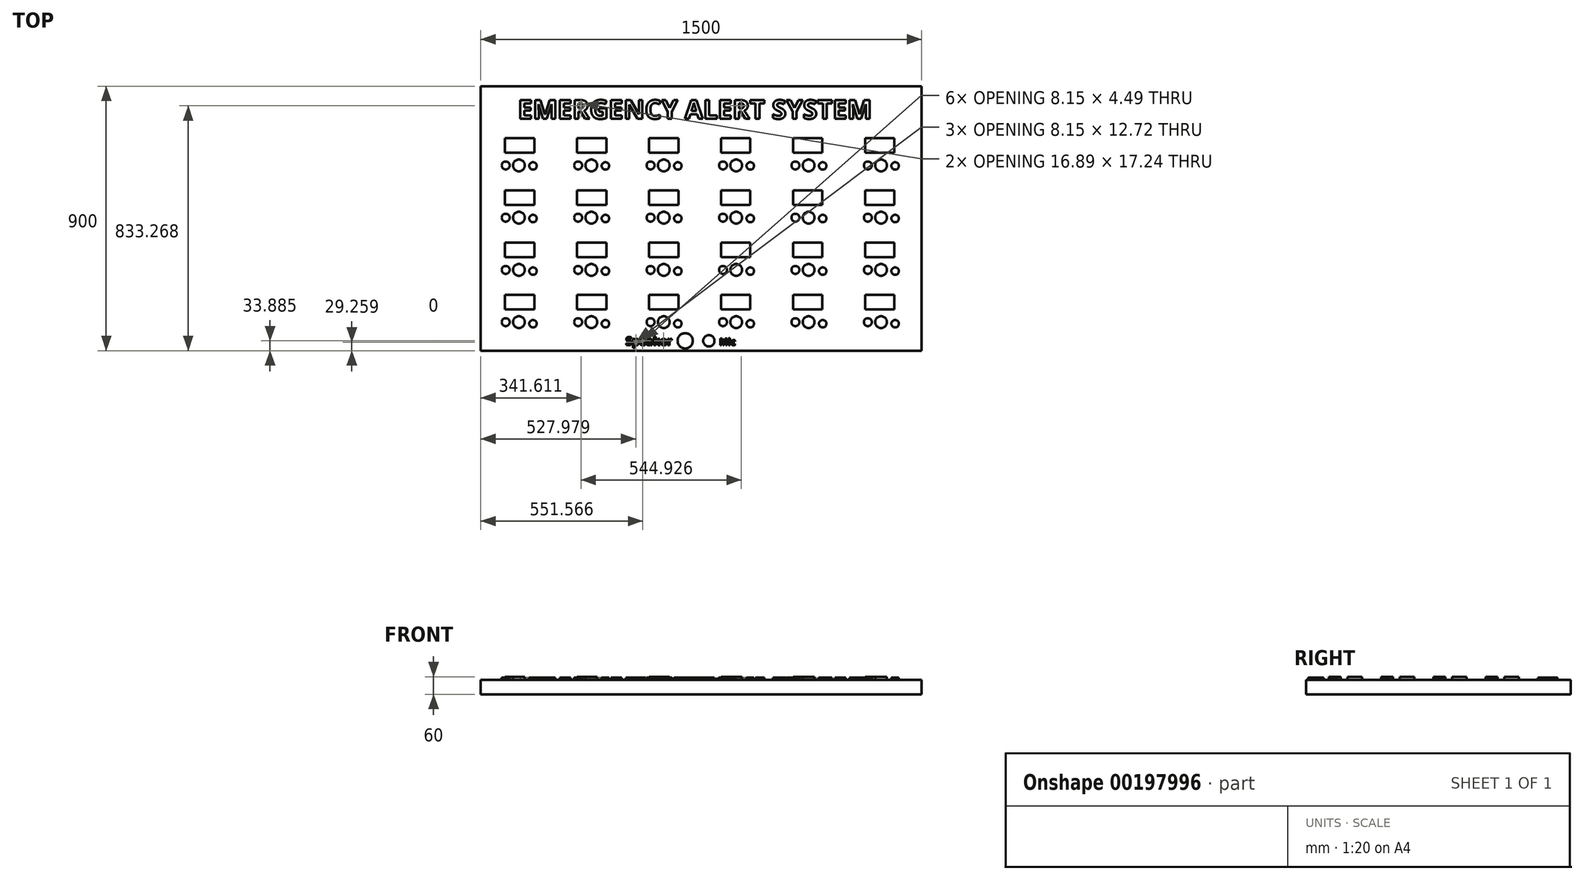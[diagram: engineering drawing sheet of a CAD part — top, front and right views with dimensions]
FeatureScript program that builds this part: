
annotation { "Feature Type Name" : "Feature", "Feature Type Description" : "" }
export const myFeature = defineFeature(function(context is Context, id is Id, definition is map)
    precondition{}
    {
        {
            var Q0;
            Q0=qCreatedBy(makeId("Top.planeOp"),FACE);
            var sketch = newSketch(context, id + "F0", { "sketchPlane" : qUnion([Q0])});
            skLineSegment(sketch, "E0.bottom", {"start": v(-750, 450) * mm, "end": v(750, 450) * mm});
            skLineSegment(sketch, "E0.top", {"start": v(-750, -450) * mm, "end": v(750, -450) * mm});
            skLineSegment(sketch, "E0.left", {"start": v(-750, 450) * mm, "end": v(-750, -450) * mm});
            skLineSegment(sketch, "E0.right", {"start": v(750, 450) * mm, "end": v(750, -450) * mm});
            skPoint(sketch, "E0.middle", {"position": v(0, 0) * mm});
            skSolve(sketch);
        }
        {
            var Q0;
            Q0=makeQuery(id+"F0.imprint","IMPRINT",FACE,{"disambiguationData":[TD([[makeQuery(id+"F0.imprint","IMPRINT",EDGE,{"derivedFrom":sQuery(id+"F0.wireOp",EDGE,"E0.bottom")}),-1.0]])]});
            extrude(context, id + "F1", {"entities" : qUnion([Q0]), "depth" : 50 * mm});
        }
        {
            var Q0;
            Q0=makeQuery(id+"F1.opExtrude","CAP_FACE",FACE,{"disambiguationData":[OSD([sQuery(id+"F0.wireOp",EDGE,"E0.bottom"),sQuery(id+"F0.wireOp",EDGE,"E0.top"),sQuery(id+"F0.wireOp",EDGE,"E0.left"),sQuery(id+"F0.wireOp",EDGE,"E0.right")])],"isStart":false});
            var sketch = newSketch(context, id + "F2", { "sketchPlane" : qUnion([Q0])});
            skLineSegment(sketch, "E1.bottom", {"start": v(-667.65, 273.63) * mm, "end": v(-567.65, 273.63) * mm});
            skLineSegment(sketch, "E1.top", {"start": v(-667.65, 223.63) * mm, "end": v(-567.65, 223.63) * mm});
            skLineSegment(sketch, "E1.left", {"start": v(-667.65, 273.63) * mm, "end": v(-667.65, 223.63) * mm});
            skLineSegment(sketch, "E1.right", {"start": v(-567.65, 273.63) * mm, "end": v(-567.65, 223.63) * mm});
            skLineSegment(sketch, "E2.0.1.0", {"start": v(-667.65, 95.83) * mm, "end": v(-567.65, 95.83) * mm});
            skLineSegment(sketch, "E2.0.1.1", {"start": v(-567.65, 95.83) * mm, "end": v(-567.65, 45.83) * mm});
            skLineSegment(sketch, "E2.0.1.2", {"start": v(-667.65, 45.83) * mm, "end": v(-567.65, 45.83) * mm});
            skLineSegment(sketch, "E2.0.1.3", {"start": v(-667.65, 95.83) * mm, "end": v(-667.65, 45.83) * mm});
            skLineSegment(sketch, "E2.0.2.0", {"start": v(-667.65, -81.97) * mm, "end": v(-567.65, -81.97) * mm});
            skLineSegment(sketch, "E2.0.2.1", {"start": v(-567.65, -81.97) * mm, "end": v(-567.65, -131.97) * mm});
            skLineSegment(sketch, "E2.0.2.2", {"start": v(-667.65, -131.97) * mm, "end": v(-567.65, -131.97) * mm});
            skLineSegment(sketch, "E2.0.2.3", {"start": v(-667.65, -81.97) * mm, "end": v(-667.65, -131.97) * mm});
            skLineSegment(sketch, "E2.0.3.0", {"start": v(-667.65, -259.77) * mm, "end": v(-567.65, -259.77) * mm});
            skLineSegment(sketch, "E2.0.3.1", {"start": v(-567.65, -259.77) * mm, "end": v(-567.65, -309.77) * mm});
            skLineSegment(sketch, "E2.0.3.2", {"start": v(-667.65, -309.77) * mm, "end": v(-567.65, -309.77) * mm});
            skLineSegment(sketch, "E2.0.3.3", {"start": v(-667.65, -259.77) * mm, "end": v(-667.65, -309.77) * mm});
            skLineSegment(sketch, "E2.1.0.0", {"start": v(-422.65, 273.63) * mm, "end": v(-322.65, 273.63) * mm});
            skLineSegment(sketch, "E2.1.0.1", {"start": v(-322.65, 273.63) * mm, "end": v(-322.65, 223.63) * mm});
            skLineSegment(sketch, "E2.1.0.2", {"start": v(-422.65, 223.63) * mm, "end": v(-322.65, 223.63) * mm});
            skLineSegment(sketch, "E2.1.0.3", {"start": v(-422.65, 273.63) * mm, "end": v(-422.65, 223.63) * mm});
            skLineSegment(sketch, "E2.1.1.0", {"start": v(-422.65, 95.83) * mm, "end": v(-322.65, 95.83) * mm});
            skLineSegment(sketch, "E2.1.1.1", {"start": v(-322.65, 95.83) * mm, "end": v(-322.65, 45.83) * mm});
            skLineSegment(sketch, "E2.1.1.2", {"start": v(-422.65, 45.83) * mm, "end": v(-322.65, 45.83) * mm});
            skLineSegment(sketch, "E2.1.1.3", {"start": v(-422.65, 95.83) * mm, "end": v(-422.65, 45.83) * mm});
            skLineSegment(sketch, "E2.1.2.0", {"start": v(-422.65, -81.97) * mm, "end": v(-322.65, -81.97) * mm});
            skLineSegment(sketch, "E2.1.2.1", {"start": v(-322.65, -81.97) * mm, "end": v(-322.65, -131.97) * mm});
            skLineSegment(sketch, "E2.1.2.2", {"start": v(-422.65, -131.97) * mm, "end": v(-322.65, -131.97) * mm});
            skLineSegment(sketch, "E2.1.2.3", {"start": v(-422.65, -81.97) * mm, "end": v(-422.65, -131.97) * mm});
            skLineSegment(sketch, "E2.1.3.0", {"start": v(-422.65, -259.77) * mm, "end": v(-322.65, -259.77) * mm});
            skLineSegment(sketch, "E2.1.3.1", {"start": v(-322.65, -259.77) * mm, "end": v(-322.65, -309.77) * mm});
            skLineSegment(sketch, "E2.1.3.2", {"start": v(-422.65, -309.77) * mm, "end": v(-322.65, -309.77) * mm});
            skLineSegment(sketch, "E2.1.3.3", {"start": v(-422.65, -259.77) * mm, "end": v(-422.65, -309.77) * mm});
            skLineSegment(sketch, "E2.2.0.0", {"start": v(-177.65, 273.63) * mm, "end": v(-77.65, 273.63) * mm});
            skLineSegment(sketch, "E2.2.0.1", {"start": v(-77.65, 273.63) * mm, "end": v(-77.65, 223.63) * mm});
            skLineSegment(sketch, "E2.2.0.2", {"start": v(-177.65, 223.63) * mm, "end": v(-77.65, 223.63) * mm});
            skLineSegment(sketch, "E2.2.0.3", {"start": v(-177.65, 273.63) * mm, "end": v(-177.65, 223.63) * mm});
            skLineSegment(sketch, "E2.2.1.0", {"start": v(-177.65, 95.83) * mm, "end": v(-77.65, 95.83) * mm});
            skLineSegment(sketch, "E2.2.1.1", {"start": v(-77.65, 95.83) * mm, "end": v(-77.65, 45.83) * mm});
            skLineSegment(sketch, "E2.2.1.2", {"start": v(-177.65, 45.83) * mm, "end": v(-77.65, 45.83) * mm});
            skLineSegment(sketch, "E2.2.1.3", {"start": v(-177.65, 95.83) * mm, "end": v(-177.65, 45.83) * mm});
            skLineSegment(sketch, "E2.2.2.0", {"start": v(-177.65, -81.97) * mm, "end": v(-77.65, -81.97) * mm});
            skLineSegment(sketch, "E2.2.2.1", {"start": v(-77.65, -81.97) * mm, "end": v(-77.65, -131.97) * mm});
            skLineSegment(sketch, "E2.2.2.2", {"start": v(-177.65, -131.97) * mm, "end": v(-77.65, -131.97) * mm});
            skLineSegment(sketch, "E2.2.2.3", {"start": v(-177.65, -81.97) * mm, "end": v(-177.65, -131.97) * mm});
            skLineSegment(sketch, "E2.2.3.0", {"start": v(-177.65, -259.77) * mm, "end": v(-77.65, -259.77) * mm});
            skLineSegment(sketch, "E2.2.3.1", {"start": v(-77.65, -259.77) * mm, "end": v(-77.65, -309.77) * mm});
            skLineSegment(sketch, "E2.2.3.2", {"start": v(-177.65, -309.77) * mm, "end": v(-77.65, -309.77) * mm});
            skLineSegment(sketch, "E2.2.3.3", {"start": v(-177.65, -259.77) * mm, "end": v(-177.65, -309.77) * mm});
            skLineSegment(sketch, "E2.3.0.0", {"start": v(67.35, 273.63) * mm, "end": v(167.35, 273.63) * mm});
            skLineSegment(sketch, "E2.3.0.1", {"start": v(167.35, 273.63) * mm, "end": v(167.35, 223.63) * mm});
            skLineSegment(sketch, "E2.3.0.2", {"start": v(67.35, 223.63) * mm, "end": v(167.35, 223.63) * mm});
            skLineSegment(sketch, "E2.3.0.3", {"start": v(67.35, 273.63) * mm, "end": v(67.35, 223.63) * mm});
            skLineSegment(sketch, "E2.3.1.0", {"start": v(67.35, 95.83) * mm, "end": v(167.35, 95.83) * mm});
            skLineSegment(sketch, "E2.3.1.1", {"start": v(167.35, 95.83) * mm, "end": v(167.35, 45.83) * mm});
            skLineSegment(sketch, "E2.3.1.2", {"start": v(67.35, 45.83) * mm, "end": v(167.35, 45.83) * mm});
            skLineSegment(sketch, "E2.3.1.3", {"start": v(67.35, 95.83) * mm, "end": v(67.35, 45.83) * mm});
            skLineSegment(sketch, "E2.3.2.0", {"start": v(67.35, -81.97) * mm, "end": v(167.35, -81.97) * mm});
            skLineSegment(sketch, "E2.3.2.1", {"start": v(167.35, -81.97) * mm, "end": v(167.35, -131.97) * mm});
            skLineSegment(sketch, "E2.3.2.2", {"start": v(67.35, -131.97) * mm, "end": v(167.35, -131.97) * mm});
            skLineSegment(sketch, "E2.3.2.3", {"start": v(67.35, -81.97) * mm, "end": v(67.35, -131.97) * mm});
            skLineSegment(sketch, "E2.3.3.0", {"start": v(67.35, -259.77) * mm, "end": v(167.35, -259.77) * mm});
            skLineSegment(sketch, "E2.3.3.1", {"start": v(167.35, -259.77) * mm, "end": v(167.35, -309.77) * mm});
            skLineSegment(sketch, "E2.3.3.2", {"start": v(67.35, -309.77) * mm, "end": v(167.35, -309.77) * mm});
            skLineSegment(sketch, "E2.3.3.3", {"start": v(67.35, -259.77) * mm, "end": v(67.35, -309.77) * mm});
            skLineSegment(sketch, "E2.4.0.0", {"start": v(312.35, 273.63) * mm, "end": v(412.35, 273.63) * mm});
            skLineSegment(sketch, "E2.4.0.1", {"start": v(412.35, 273.63) * mm, "end": v(412.35, 223.63) * mm});
            skLineSegment(sketch, "E2.4.0.2", {"start": v(312.35, 223.63) * mm, "end": v(412.35, 223.63) * mm});
            skLineSegment(sketch, "E2.4.0.3", {"start": v(312.35, 273.63) * mm, "end": v(312.35, 223.63) * mm});
            skLineSegment(sketch, "E2.4.1.0", {"start": v(312.35, 95.83) * mm, "end": v(412.35, 95.83) * mm});
            skLineSegment(sketch, "E2.4.1.1", {"start": v(412.35, 95.83) * mm, "end": v(412.35, 45.83) * mm});
            skLineSegment(sketch, "E2.4.1.2", {"start": v(312.35, 45.83) * mm, "end": v(412.35, 45.83) * mm});
            skLineSegment(sketch, "E2.4.1.3", {"start": v(312.35, 95.83) * mm, "end": v(312.35, 45.83) * mm});
            skLineSegment(sketch, "E2.4.2.0", {"start": v(312.35, -81.97) * mm, "end": v(412.35, -81.97) * mm});
            skLineSegment(sketch, "E2.4.2.1", {"start": v(412.35, -81.97) * mm, "end": v(412.35, -131.97) * mm});
            skLineSegment(sketch, "E2.4.2.2", {"start": v(312.35, -131.97) * mm, "end": v(412.35, -131.97) * mm});
            skLineSegment(sketch, "E2.4.2.3", {"start": v(312.35, -81.97) * mm, "end": v(312.35, -131.97) * mm});
            skLineSegment(sketch, "E2.4.3.0", {"start": v(312.35, -259.77) * mm, "end": v(412.35, -259.77) * mm});
            skLineSegment(sketch, "E2.4.3.1", {"start": v(412.35, -259.77) * mm, "end": v(412.35, -309.77) * mm});
            skLineSegment(sketch, "E2.4.3.2", {"start": v(312.35, -309.77) * mm, "end": v(412.35, -309.77) * mm});
            skLineSegment(sketch, "E2.4.3.3", {"start": v(312.35, -259.77) * mm, "end": v(312.35, -309.77) * mm});
            skLineSegment(sketch, "E2.5.0.0", {"start": v(557.35, 273.63) * mm, "end": v(657.35, 273.63) * mm});
            skLineSegment(sketch, "E2.5.0.1", {"start": v(657.35, 273.63) * mm, "end": v(657.35, 223.63) * mm});
            skLineSegment(sketch, "E2.5.0.2", {"start": v(557.35, 223.63) * mm, "end": v(657.35, 223.63) * mm});
            skLineSegment(sketch, "E2.5.0.3", {"start": v(557.35, 273.63) * mm, "end": v(557.35, 223.63) * mm});
            skLineSegment(sketch, "E2.5.1.0", {"start": v(557.35, 95.83) * mm, "end": v(657.35, 95.83) * mm});
            skLineSegment(sketch, "E2.5.1.1", {"start": v(657.35, 95.83) * mm, "end": v(657.35, 45.83) * mm});
            skLineSegment(sketch, "E2.5.1.2", {"start": v(557.35, 45.83) * mm, "end": v(657.35, 45.83) * mm});
            skLineSegment(sketch, "E2.5.1.3", {"start": v(557.35, 95.83) * mm, "end": v(557.35, 45.83) * mm});
            skLineSegment(sketch, "E2.5.2.0", {"start": v(557.35, -81.97) * mm, "end": v(657.35, -81.97) * mm});
            skLineSegment(sketch, "E2.5.2.1", {"start": v(657.35, -81.97) * mm, "end": v(657.35, -131.97) * mm});
            skLineSegment(sketch, "E2.5.2.2", {"start": v(557.35, -131.97) * mm, "end": v(657.35, -131.97) * mm});
            skLineSegment(sketch, "E2.5.2.3", {"start": v(557.35, -81.97) * mm, "end": v(557.35, -131.97) * mm});
            skLineSegment(sketch, "E2.5.3.0", {"start": v(557.35, -259.77) * mm, "end": v(657.35, -259.77) * mm});
            skLineSegment(sketch, "E2.5.3.1", {"start": v(657.35, -259.77) * mm, "end": v(657.35, -309.77) * mm});
            skLineSegment(sketch, "E2.5.3.2", {"start": v(557.35, -309.77) * mm, "end": v(657.35, -309.77) * mm});
            skLineSegment(sketch, "E2.5.3.3", {"start": v(557.35, -259.77) * mm, "end": v(557.35, -309.77) * mm});
            skLineSegment(sketch, "E2.direction1", {"start": v(-667.65, 273.63) * mm, "end": v(-422.65, 273.63) * mm, "construction": true});
            skLineSegment(sketch, "E2.direction2", {"start": v(-667.65, 273.63) * mm, "end": v(-667.65, 95.83) * mm, "construction": true});
            skSolve(sketch);
        }
        {
            var Q0;
            Q0=qSketchRegion(id+"F2",true);
            extrude(context, id + "F3", {"entities" : qUnion([Q0]), "depth" : 10 * mm});
        }
        {
            var Q0;
            Q0=makeQuery(id+"F1.opExtrude","CAP_FACE",FACE,{"disambiguationData":[OSD([sQuery(id+"F0.wireOp",EDGE,"E0.bottom"),sQuery(id+"F0.wireOp",EDGE,"E0.top"),sQuery(id+"F0.wireOp",EDGE,"E0.left"),sQuery(id+"F0.wireOp",EDGE,"E0.right")])],"isStart":false});
            var sketch = newSketch(context, id + "F4", { "sketchPlane" : qUnion([Q0])});
            skCircle(sketch, "E3", {"center": v(-619.9, 180.43) * mm, "radius": 20.14 * mm});
            skCircle(sketch, "E4.0.1.0", {"center": v(-619.9, 2.63) * mm, "radius": 20.14 * mm});
            skCircle(sketch, "E4.0.2.0", {"center": v(-619.9, -175.17) * mm, "radius": 20.14 * mm});
            skCircle(sketch, "E4.0.3.0", {"center": v(-619.9, -352.97) * mm, "radius": 20.14 * mm});
            skCircle(sketch, "E4.1.0.0", {"center": v(-373.51, 180.43) * mm, "radius": 20.14 * mm});
            skCircle(sketch, "E4.1.1.0", {"center": v(-373.51, 2.63) * mm, "radius": 20.14 * mm});
            skCircle(sketch, "E4.1.2.0", {"center": v(-373.51, -175.17) * mm, "radius": 20.14 * mm});
            skCircle(sketch, "E4.1.3.0", {"center": v(-373.51, -352.97) * mm, "radius": 20.14 * mm});
            skCircle(sketch, "E4.2.0.0", {"center": v(-127.13, 180.43) * mm, "radius": 20.14 * mm});
            skCircle(sketch, "E4.2.1.0", {"center": v(-127.13, 2.63) * mm, "radius": 20.14 * mm});
            skCircle(sketch, "E4.2.2.0", {"center": v(-127.13, -175.17) * mm, "radius": 20.14 * mm});
            skCircle(sketch, "E4.2.3.0", {"center": v(-127.13, -352.97) * mm, "radius": 20.14 * mm});
            skCircle(sketch, "E4.3.0.0", {"center": v(119.25, 180.43) * mm, "radius": 20.14 * mm});
            skCircle(sketch, "E4.3.1.0", {"center": v(119.25, 2.63) * mm, "radius": 20.14 * mm});
            skCircle(sketch, "E4.3.2.0", {"center": v(119.25, -175.17) * mm, "radius": 20.14 * mm});
            skCircle(sketch, "E4.3.3.0", {"center": v(119.25, -352.97) * mm, "radius": 20.14 * mm});
            skCircle(sketch, "E4.4.0.0", {"center": v(365.63, 180.43) * mm, "radius": 20.14 * mm});
            skCircle(sketch, "E4.4.1.0", {"center": v(365.63, 2.63) * mm, "radius": 20.14 * mm});
            skCircle(sketch, "E4.4.2.0", {"center": v(365.63, -175.17) * mm, "radius": 20.14 * mm});
            skCircle(sketch, "E4.4.3.0", {"center": v(365.63, -352.97) * mm, "radius": 20.14 * mm});
            skCircle(sketch, "E4.5.0.0", {"center": v(612, 180.43) * mm, "radius": 20.14 * mm});
            skCircle(sketch, "E4.5.1.0", {"center": v(612, 2.63) * mm, "radius": 20.14 * mm});
            skCircle(sketch, "E4.5.2.0", {"center": v(612, -175.17) * mm, "radius": 20.14 * mm});
            skCircle(sketch, "E4.5.3.0", {"center": v(612, -352.97) * mm, "radius": 20.14 * mm});
            skLineSegment(sketch, "E4.direction1", {"start": v(-619.9, 180.43) * mm, "end": v(-373.51, 180.43) * mm, "construction": true});
            skLineSegment(sketch, "E4.direction2", {"start": v(-619.9, 180.43) * mm, "end": v(-619.9, 2.63) * mm, "construction": true});
            skSolve(sketch);
        }
        {
            var Q0;
            Q0=qSketchRegion(id+"F4",true);
            extrude(context, id + "F5", {"entities" : qUnion([Q0]), "depth" : 10 * mm});
        }
        {
            var Q0;
            Q0=makeQuery(id+"F1.opExtrude","CAP_FACE",FACE,{"disambiguationData":[OSD([sQuery(id+"F0.wireOp",EDGE,"E0.bottom"),sQuery(id+"F0.wireOp",EDGE,"E0.top"),sQuery(id+"F0.wireOp",EDGE,"E0.left"),sQuery(id+"F0.wireOp",EDGE,"E0.right")])],"isStart":false});
            var sketch = newSketch(context, id + "F6", { "sketchPlane" : qUnion([Q0])});
            skSolve(sketch);
        }
        {
            var Q0;
            Q0=makeQuery(id+"F6.imprint","IMPRINT",FACE,{"disambiguationData":[TD([[makeQuery(id+"F6.imprint","IMPRINT",EDGE,{"derivedFrom":makeQuery(id+"F1.opExtrude","CAP_EDGE",EDGE,{"disambiguationData":[OSD([sQuery(id+"F0.wireOp",EDGE,"E0.bottom")])],"isStart":false})}),-1.0]])]});
            var sketch = newSketch(context, id + "F7", { "sketchPlane" : qUnion([Q0])});
            skCircle(sketch, "E5", {"center": v(-571.98, 178.93) * mm, "radius": 12.7 * mm});
            skCircle(sketch, "E6.0.1.0", {"center": v(-571.98, -0.14) * mm, "radius": 12.7 * mm});
            skCircle(sketch, "E6.0.2.0", {"center": v(-571.98, -179.2) * mm, "radius": 12.7 * mm});
            skCircle(sketch, "E6.0.3.0", {"center": v(-571.98, -358.28) * mm, "radius": 12.7 * mm});
            skCircle(sketch, "E6.1.0.0", {"center": v(-325.6, 178.93) * mm, "radius": 12.7 * mm});
            skCircle(sketch, "E6.1.1.0", {"center": v(-325.6, -0.14) * mm, "radius": 12.7 * mm});
            skCircle(sketch, "E6.1.2.0", {"center": v(-325.6, -179.2) * mm, "radius": 12.7 * mm});
            skCircle(sketch, "E6.1.3.0", {"center": v(-325.6, -358.28) * mm, "radius": 12.7 * mm});
            skCircle(sketch, "E6.2.0.0", {"center": v(-79.22, 178.93) * mm, "radius": 12.7 * mm});
            skCircle(sketch, "E6.2.1.0", {"center": v(-79.22, -0.14) * mm, "radius": 12.7 * mm});
            skCircle(sketch, "E6.2.2.0", {"center": v(-79.22, -179.2) * mm, "radius": 12.7 * mm});
            skCircle(sketch, "E6.2.3.0", {"center": v(-79.22, -358.28) * mm, "radius": 12.7 * mm});
            skCircle(sketch, "E6.3.0.0", {"center": v(167.16, 178.93) * mm, "radius": 12.7 * mm});
            skCircle(sketch, "E6.3.1.0", {"center": v(167.16, -0.14) * mm, "radius": 12.7 * mm});
            skCircle(sketch, "E6.3.2.0", {"center": v(167.16, -179.2) * mm, "radius": 12.7 * mm});
            skCircle(sketch, "E6.3.3.0", {"center": v(167.16, -358.28) * mm, "radius": 12.7 * mm});
            skCircle(sketch, "E6.4.0.0", {"center": v(413.54, 178.93) * mm, "radius": 12.7 * mm});
            skCircle(sketch, "E6.4.1.0", {"center": v(413.54, -0.14) * mm, "radius": 12.7 * mm});
            skCircle(sketch, "E6.4.2.0", {"center": v(413.54, -179.2) * mm, "radius": 12.7 * mm});
            skCircle(sketch, "E6.4.3.0", {"center": v(413.54, -358.28) * mm, "radius": 12.7 * mm});
            skCircle(sketch, "E6.5.0.0", {"center": v(659.92, 178.93) * mm, "radius": 12.7 * mm});
            skCircle(sketch, "E6.5.1.0", {"center": v(659.92, -0.14) * mm, "radius": 12.7 * mm});
            skCircle(sketch, "E6.5.2.0", {"center": v(659.92, -179.2) * mm, "radius": 12.7 * mm});
            skCircle(sketch, "E6.5.3.0", {"center": v(659.92, -358.28) * mm, "radius": 12.7 * mm});
            skLineSegment(sketch, "E6.direction1", {"start": v(-571.98, 178.93) * mm, "end": v(-325.6, 178.93) * mm, "construction": true});
            skLineSegment(sketch, "E6.direction2", {"start": v(-571.98, 178.93) * mm, "end": v(-571.98, -0.14) * mm, "construction": true});
            skSolve(sketch);
        }
        {
            var Q0;
            Q0=qSketchRegion(id+"F7",true);
            extrude(context, id + "F8", {"entities" : qUnion([Q0]), "depth" : 7 * mm});
        }
        {
            var Q0;
            Q0=makeQuery(id+"F6.imprint","IMPRINT",FACE,{"disambiguationData":[TD([[makeQuery(id+"F6.imprint","IMPRINT",EDGE,{"derivedFrom":makeQuery(id+"F1.opExtrude","CAP_EDGE",EDGE,{"disambiguationData":[OSD([sQuery(id+"F0.wireOp",EDGE,"E0.bottom")])],"isStart":false})}),-1.0]])]});
            var sketch = newSketch(context, id + "F9", { "sketchPlane" : qUnion([Q0])});
            skCircle(sketch, "E7", {"center": v(-664.81, 180.43) * mm, "radius": 13.56 * mm});
            skCircle(sketch, "E8.0.1.0", {"center": v(-664.81, 2.63) * mm, "radius": 13.56 * mm});
            skCircle(sketch, "E8.0.2.0", {"center": v(-664.81, -175.17) * mm, "radius": 13.56 * mm});
            skCircle(sketch, "E8.0.3.0", {"center": v(-664.81, -352.97) * mm, "radius": 13.56 * mm});
            skCircle(sketch, "E8.1.0.0", {"center": v(-418.43, 180.43) * mm, "radius": 13.56 * mm});
            skCircle(sketch, "E8.1.1.0", {"center": v(-418.43, 2.63) * mm, "radius": 13.56 * mm});
            skCircle(sketch, "E8.1.2.0", {"center": v(-418.43, -175.17) * mm, "radius": 13.56 * mm});
            skCircle(sketch, "E8.1.3.0", {"center": v(-418.43, -352.97) * mm, "radius": 13.56 * mm});
            skCircle(sketch, "E8.2.0.0", {"center": v(-172.05, 180.43) * mm, "radius": 13.56 * mm});
            skCircle(sketch, "E8.2.1.0", {"center": v(-172.05, 2.63) * mm, "radius": 13.56 * mm});
            skCircle(sketch, "E8.2.2.0", {"center": v(-172.05, -175.17) * mm, "radius": 13.56 * mm});
            skCircle(sketch, "E8.2.3.0", {"center": v(-172.05, -352.97) * mm, "radius": 13.56 * mm});
            skCircle(sketch, "E8.3.0.0", {"center": v(74.33, 180.43) * mm, "radius": 13.56 * mm});
            skCircle(sketch, "E8.3.1.0", {"center": v(74.33, 2.63) * mm, "radius": 13.56 * mm});
            skCircle(sketch, "E8.3.2.0", {"center": v(74.33, -175.17) * mm, "radius": 13.56 * mm});
            skCircle(sketch, "E8.3.3.0", {"center": v(74.33, -352.97) * mm, "radius": 13.56 * mm});
            skCircle(sketch, "E8.4.0.0", {"center": v(320.7, 180.43) * mm, "radius": 13.56 * mm});
            skCircle(sketch, "E8.4.1.0", {"center": v(320.7, 2.63) * mm, "radius": 13.56 * mm});
            skCircle(sketch, "E8.4.2.0", {"center": v(320.7, -175.17) * mm, "radius": 13.56 * mm});
            skCircle(sketch, "E8.4.3.0", {"center": v(320.7, -352.97) * mm, "radius": 13.56 * mm});
            skCircle(sketch, "E8.5.0.0", {"center": v(567.09, 180.43) * mm, "radius": 13.56 * mm});
            skCircle(sketch, "E8.5.1.0", {"center": v(567.09, 2.63) * mm, "radius": 13.56 * mm});
            skCircle(sketch, "E8.5.2.0", {"center": v(567.09, -175.17) * mm, "radius": 13.56 * mm});
            skCircle(sketch, "E8.5.3.0", {"center": v(567.09, -352.97) * mm, "radius": 13.56 * mm});
            skLineSegment(sketch, "E8.direction1", {"start": v(-664.81, 180.43) * mm, "end": v(-418.43, 180.43) * mm, "construction": true});
            skLineSegment(sketch, "E8.direction2", {"start": v(-664.81, 180.43) * mm, "end": v(-664.81, 2.63) * mm, "construction": true});
            skSolve(sketch);
        }
        {
            var Q0;
            Q0=qSketchRegion(id+"F9",true);
            extrude(context, id + "F10", {"entities" : qUnion([Q0]), "depth" : 7 * mm});
        }
        {
            var Q0;
            Q0=makeQuery(id+"F6.imprint","IMPRINT",FACE,{"disambiguationData":[TD([[makeQuery(id+"F6.imprint","IMPRINT",EDGE,{"derivedFrom":makeQuery(id+"F1.opExtrude","CAP_EDGE",EDGE,{"disambiguationData":[OSD([sQuery(id+"F0.wireOp",EDGE,"E0.bottom")])],"isStart":false})}),-1.0]])]});
            var sketch = newSketch(context, id + "F11", { "sketchPlane" : qUnion([Q0])});
            skText(sketch, "E9", { "text": "EMERGENCY ALERT SYSTEM", "fontName": "OpenSans-Bold.ttf"});
            const initialGuessF11  = {"E9": [-0.62289, 0.33914, 1, 0, 0.06439]};
            skSetInitialGuess(sketch, initialGuessF11);
            skSolve(sketch);
        }
        {
            var Q0;
            Q0=qSketchRegion(id+"F11",true);
            extrude(context, id + "F12", {"entities" : qUnion([Q0]), "depth" : 7 * mm});
        }
        {
            var Q0;
            Q0=makeQuery(id+"F6.imprint","IMPRINT",FACE,{"disambiguationData":[TD([[makeQuery(id+"F6.imprint","IMPRINT",EDGE,{"derivedFrom":makeQuery(id+"F1.opExtrude","CAP_EDGE",EDGE,{"disambiguationData":[OSD([sQuery(id+"F0.wireOp",EDGE,"E0.bottom")])],"isStart":false})}),-1.0]])]});
            var sketch = newSketch(context, id + "F13", { "sketchPlane" : qUnion([Q0])});
            skCircle(sketch, "E10", {"center": v(-54.28, -416.44) * mm, "radius": 26 * mm});
            skSolve(sketch);
        }
        {
            var Q0;
            Q0=qSketchRegion(id+"F13",true);
            extrude(context, id + "F14", {"entities" : qUnion([Q0]), "depth" : 7 * mm});
        }
        {
            var Q0;
            Q0=makeQuery(id+"F6.imprint","IMPRINT",FACE,{"disambiguationData":[TD([[makeQuery(id+"F6.imprint","IMPRINT",EDGE,{"derivedFrom":makeQuery(id+"F1.opExtrude","CAP_EDGE",EDGE,{"disambiguationData":[OSD([sQuery(id+"F0.wireOp",EDGE,"E0.bottom")])],"isStart":false})}),-1.0]])]});
            var sketch = newSketch(context, id + "F15", { "sketchPlane" : qUnion([Q0])});
            skCircle(sketch, "E11", {"center": v(26.2, -416.44) * mm, "radius": 19.27 * mm});
            skSolve(sketch);
        }
        {
            var Q0;
            Q0=qSketchRegion(id+"F15",true);
            extrude(context, id + "F16", {"entities" : qUnion([Q0]), "depth" : 7 * mm});
        }
        {
            var Q0;
            Q0=makeQuery(id+"F6.imprint","IMPRINT",FACE,{"disambiguationData":[TD([[makeQuery(id+"F6.imprint","IMPRINT",EDGE,{"derivedFrom":makeQuery(id+"F1.opExtrude","CAP_EDGE",EDGE,{"disambiguationData":[OSD([sQuery(id+"F0.wireOp",EDGE,"E0.bottom")])],"isStart":false})}),-1.0]])]});
            var sketch = newSketch(context, id + "F17", { "sketchPlane" : qUnion([Q0])});
            skText(sketch, "E12", { "text": "Speaker", "fontName": "OpenSans-Bold.ttf"});
            const initialGuessF17  = {"E12": [-0.25642, -0.43142, 1, 0, 0.02807]};
            skSetInitialGuess(sketch, initialGuessF17);
            skSolve(sketch);
        }
        {
            var Q0;
            Q0=qSketchRegion(id+"F17",true);
            extrude(context, id + "F18", {"entities" : qUnion([Q0]), "depth" : 7 * mm});
        }
        {
            var Q0;
            Q0=makeQuery(id+"F6.imprint","IMPRINT",FACE,{"disambiguationData":[TD([[makeQuery(id+"F6.imprint","IMPRINT",EDGE,{"derivedFrom":makeQuery(id+"F1.opExtrude","CAP_EDGE",EDGE,{"disambiguationData":[OSD([sQuery(id+"F0.wireOp",EDGE,"E0.bottom")])],"isStart":false})}),-1.0]])]});
            var sketch = newSketch(context, id + "F19", { "sketchPlane" : qUnion([Q0])});
            skText(sketch, "E13", { "text": "Mic", "fontName": "OpenSans-Bold.ttf"});
            const initialGuessF19  = {"E13": [0.06176, -0.43142, 1, 0, 0.02246]};
            skSetInitialGuess(sketch, initialGuessF19);
            skSolve(sketch);
        }
        {
            var Q0;
            Q0=qSketchRegion(id+"F19",true);
            extrude(context, id + "F20", {"entities" : qUnion([Q0]), "depth" : 7 * mm});
        }
        {
            var Q0;
            Q0=qSketchRegion(id+"F17",true);
            extrude(context, id + "F21", {"entities" : qUnion([Q0]), "depth" : 7 * mm});
        }
        {
            var Q0;
            Q0=qSketchRegion(id+"F17",true);
            extrude(context, id + "F22", {"entities" : qUnion([Q0]), "depth" : 7 * mm});
        }
    });
